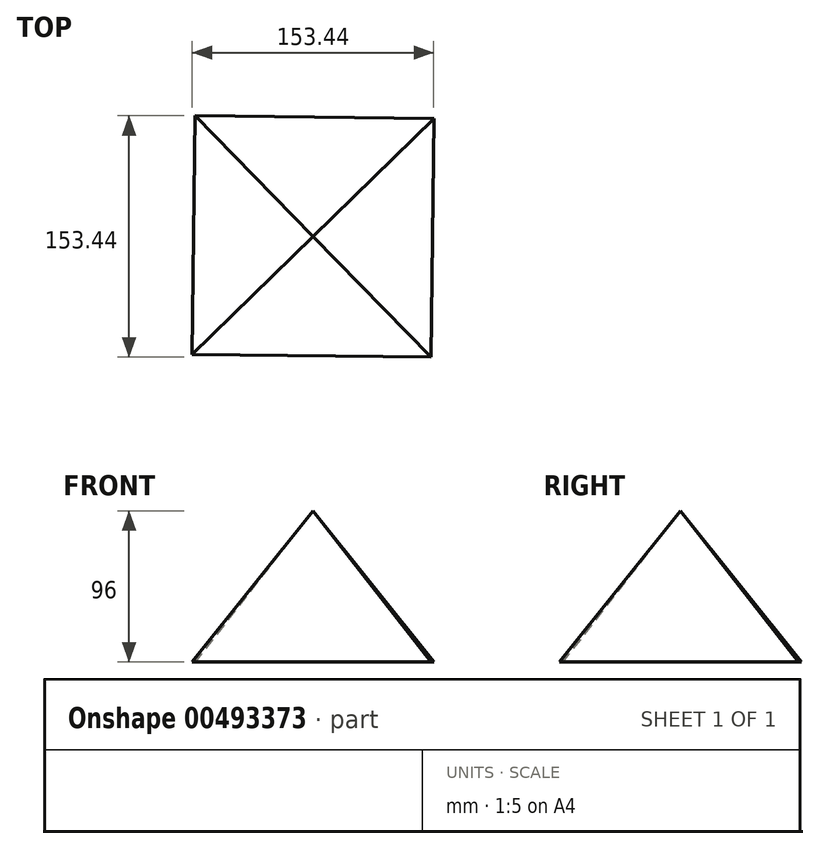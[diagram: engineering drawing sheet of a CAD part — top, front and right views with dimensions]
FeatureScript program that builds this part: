
annotation { "Feature Type Name" : "Feature", "Feature Type Description" : "" }
export const myFeature = defineFeature(function(context is Context, id is Id, definition is map)
    precondition{}
    {
        {
            var Q0;
            Q0=qCreatedBy(makeId("Top.planeOp"),FACE);
            var sketch = newSketch(context, id + "F0", { "sketchPlane" : qUnion([Q0])});
            skCircle(sketch, "E0.cCircle", {"center": v(0, 0) * mm, "radius": 107.22 * mm, "construction": true});
            skLineSegment(sketch, "E0.0", {"start": v(-74.9, 76.72) * mm, "end": v(76.72, 74.9) * mm});
            skLineSegment(sketch, "E0.1", {"start": v(76.72, 74.9) * mm, "end": v(74.9, -76.72) * mm});
            skLineSegment(sketch, "E0.2", {"start": v(74.9, -76.72) * mm, "end": v(-76.72, -74.9) * mm});
            skLineSegment(sketch, "E0.3", {"start": v(-76.72, -74.9) * mm, "end": v(-74.9, 76.72) * mm});
            skSolve(sketch);
        }
        {
            var Q0;
            Q0=qCreatedBy(makeId("Top.planeOp"),FACE);
            cPlane(context, id + "F1", {"entities" : qUnion([Q0]), "cplaneType" : CPlaneType.OFFSET, "offset" : 96 * mm, "width" : 150 * mm, "height" : 150 * mm});
        }
        {
            var Q0;
            Q0=qCreatedBy(id+"F1.planeOp",FACE);
            var sketch = newSketch(context, id + "F2", { "sketchPlane" : qUnion([Q0])});
            skPoint(sketch, "E1", {"position": v(0, 0) * mm});
            skSolve(sketch);
        }
        {
            var Q0;
            Q0=sQuery(id+"F2.wireOp",VERTEX,"E1");
            var Q1;
            Q1=makeQuery(id+"F0.imprint","IMPRINT",FACE,{"disambiguationData":[TD([[makeQuery(id+"F0.imprint","IMPRINT",EDGE,{"derivedFrom":sQuery(id+"F0.wireOp",EDGE,"E0.0")}),-1.0]])]});
            loft(context, id + "F3", {"sheetProfilesArray" : [{ "sheetProfileEntities" : qUnion([Q0]) }, { "sheetProfileEntities" : qUnion([Q1]) }]});
        }
    });
